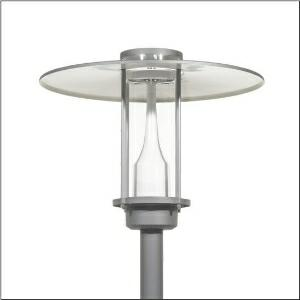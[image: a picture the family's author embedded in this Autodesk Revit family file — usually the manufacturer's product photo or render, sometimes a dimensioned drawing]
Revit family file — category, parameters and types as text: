
# Revit family: city-light_plus_iq___st1_2a_5xa5275af14hp_3410
name_source: partatom
category: Lighting Fixtures
units: mm (PartAtom-declared; Revit-internal decimal feet)

## family parameters
Cut with Voids When Loaded = No
Host = Face
Light Source = No
Part Type = Normal
Room Calculation Point = No
Round Connector Dimension = Use Diameter
Shared = No

## types (1)
- --- (1 x LED, 3730 lm, 33.6 W, 2200K)
    Apparent Load = 34 VA
    CIE Flux Codes = 22 60 93 97 100
    Color Rendering = 70
    Color Temperature = 2200K
    Default Elevation = 1800 mm
    Description = City-Light Plus iQ, mast luminaire, Module 540 iQ-SR, primary light control with 3 zone facetted reflector, of plastic, silver coated, highly specular, structured, primary optical cover: cover, of PMMA, transparent, light distribution: ST1.2a, light emission: direct distribution, primary light characteristic: asymmetric, installation type: post-top, LED, High Power LED, rated luminous flux: 3.730lm, luminous efficacy: 111lm/W, light colour: 722, colour temperature: 2200K, control gear: iQ Street-Remote, control: pre-setting: logarithmic dimming characteristic, Street-Remote, Auto-Match, Temp-Guard, Lumen-Switch, Night-Set, Smart-Wire, Light-Fading, Desk-Remote (wireless, voltage-free reading and setting of iQ features in the workshop via application-optimized NFC function/RFID function), optimised constant luminous flux control (CLO 2.0), with terminal, 6-pole, max. 2.5mm², mains connection: 230..240V, AC, 50/60Hz, start of lifetime: 34W, end of service life: 36W, reduction: 15W, luminaire housing, upper part, of glass-fibre reinforced polyester, coated, Siteco® metallic grey (DB 702S), diameter: 750mm, height: 590mm, spigot size: d x l = 76 x 70mm (post-top) | with reducer (optional accessory) 60 x 70mm, mounting height: 3..5m, post-top mast mounting element, of diecast aluminium, coated, Siteco® metallic grey (DB 702S), Module 540 iQ-SR, traffic white (RAL 9016), equipment: Power, protection rating (complete): IP65, insulation class (complete): insulation class II (safety insulation), certification: CE, ENEC, VDE, packaging unit: 1 piece

Light Distribution: ST1.2a
    Height = 590 mm
    Lamp = 1 x LED
    Lamp Light Flux = 3730 lm
    Lamp Power = 33.6 W
    Lamp count = 1
    Length = 750 mm
    Luminous efficacy = 111 lm/W
    Manufacturer = Siteco
    ModVariant = No
    Model = 5XA5275AF14HP
    Number of Poles = 1
    OnlyDefault = Yes
    Power Factor = 1
    Product Name = City-Light Plus iQ | ST1.2a
    Product group = mast luminaire | pylon top
    ProductGroupID = 6100
    Protection Class = Protection class II
    Protection Degree = IP 65
    RLX_Detail_Level = 1
    RLX_Emergency_Light_Flux = 0 lm
    RLX_Emergency_Type = 0
    RLX_Emergency_Type_DB = No
    RlxData = <blob elided: 34981 chars, md5=3133c656>
    Socket = socket
    Standby Power = 0 W
    System Light Flux = 3730 lm
    System Power = 34 W
    Type Comments = factory setting: luminous flux: 100 % | dim-lin: 254 | 695 mA
    Type Image = l_1006456.jpg
    URL = http://relux.com
    VarID = @adj_215187
    Voltage = 0 V
    Weight = 0.00 kg
    Width = 0 mm  [stored 0 ft]

note: [stored X ft] marks values corroborated as IEEE doubles in the binary element streams (Revit-internal decimal feet)

## geometry (parser evidence)
native form markers: Blend x4, Sweep x7
no freeform markers — native parametric forms only
